# Revit family: Fuentes de alimentación conmutadas_Aguilera Electronica
name_source: partatom
category: Equipos eléctricos
revit_build: Autodesk Revit 2017 (Build: 20160225_1515(x64)
units: mm (PartAtom-declared; Revit-internal decimal feet)

## family parameters
Anfitrión = Cara
Compartido = No
Corte con vacíos al cargar = No
Cota de conector redondo = Diámetro de uso
Número OmniClass = 23.85.30.21.11.14
Punto de cálculo de habitación = No
Tipo de pieza = Cuadro conmutador
Título OmniClass = Alarm Panels

## types (2) — shared parameters
Diámetro tubo = 20 mm  [stored 0.0656168 ft]
Elevación por defecto = 1200 mm
Fabricante = Aguilera Electrónica
Potencial eléctrico = 230 V
Símbolo = Sí
Símbolo texto modelo = Sí
URL = http://aguilera.es

## per-type parameters (varying)
| type | Alto | Ancho | Comentarios de tipo | Descripción | Fondo | Modelo | Potencial aparente |
| Fuente de alimentación conmutada 5A a 24V | 440 mm  [stored 1.44357 ft] | 390 mm  [stored 1.27953 ft] | 5A a 24V | Fuente de alimentación conmutada 24Vcc / 5A fabricada según norma EN 54-4.
Bitensión 230/115 Vca; 50/60Hz. Fuente alimentación cortocircuitable, provista de indicaciones luminosas del estado general de la fuente de alimentación, estado y carga de las baterías y de los fusibles de salida según norma EN 54.4.
Dispone de 2 salidas independientes protegidas contra cortocircuitos. Equipa una tarjeta microprocesada que mantiene informada a la central Algorítmica de su estado permanente. | 100 mm  [stored 0.328084 ft] | AE/SA-FA | 1150 VA |
| Fuente de alimentación conmutada 2A a 24V | 272 mm  [stored 0.892388 ft] | 320 mm  [stored 1.04987 ft] | 2A a 24V | Fuente de alimentación conmutada 24Vcc / 2A fabricada según norma EN 54-4.
Bitensión 230/115 Vca; 50/60Hz. Fuente alimentación cortocircuitable, provista de indicaciones luminosas del estado general de la fuente de alimentación, estado y carga de las baterías y de los fusibles de salida según norma EN 54.4.
Dispone de 2 salidas independientes protegidas contra cortocircuitos. Equipa una tarjeta microprocesada que mantiene informada a la central Algorítmica de su estado permanente. | 125 mm  [stored 0.410105 ft] | AE/SA-FA2 | 460 VA |

note: [stored X ft] marks values corroborated as IEEE doubles in the binary element streams (Revit-internal decimal feet)
